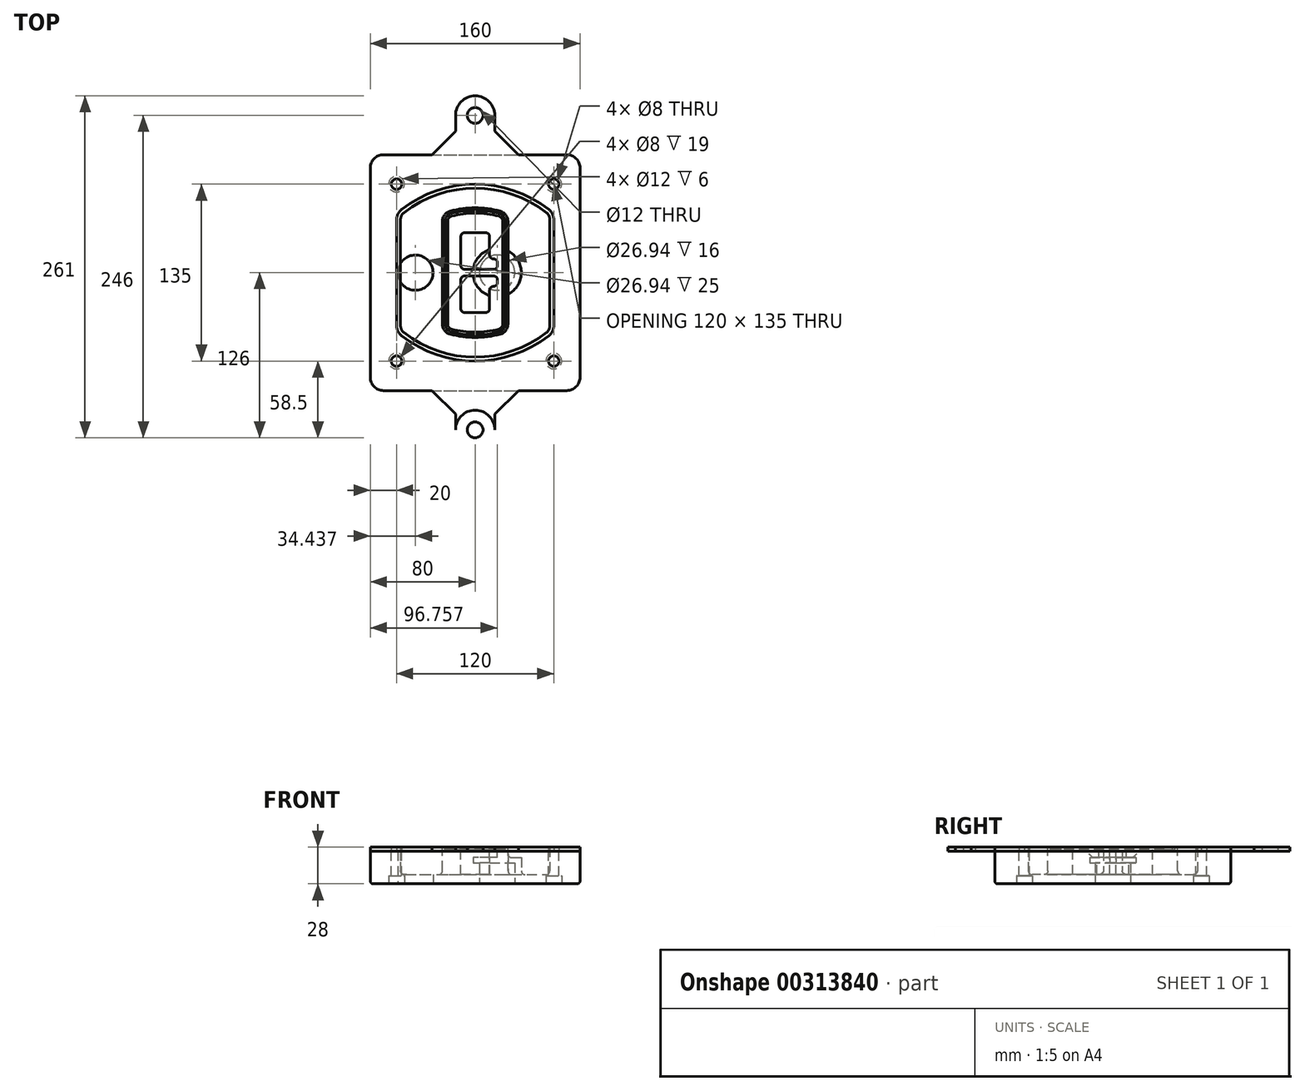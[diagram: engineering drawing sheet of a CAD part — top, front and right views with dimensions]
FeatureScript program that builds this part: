
annotation { "Feature Type Name" : "Feature", "Feature Type Description" : "" }
export const myFeature = defineFeature(function(context is Context, id is Id, definition is map)
    precondition{}
    {
        {
            var Q0;
            Q0=qCreatedBy(makeId("Top.planeOp"),FACE);
            var sketch = newSketch(context, id + "F0", { "sketchPlane" : qUnion([Q0])});
            skPoint(sketch, "E0.rect.middle", {"position": v(0, 0) * mm});
            skLineSegment(sketch, "E1.bottom", {"start": v(-70, -90) * mm, "end": v(70, -90) * mm});
            skLineSegment(sketch, "E1.top", {"start": v(-70, 90) * mm, "end": v(70, 90) * mm});
            skLineSegment(sketch, "E1.left", {"start": v(-80, -80) * mm, "end": v(-80, 80) * mm});
            skLineSegment(sketch, "E1.right", {"start": v(80, -80) * mm, "end": v(80, 80) * mm});
            skLineSegment(sketch, "E2", {"start": v(-80, 90) * mm, "end": v(80, -90) * mm, "construction": true});
            skLineSegment(sketch, "E3", {"start": v(80, 90) * mm, "end": v(-80, -90) * mm, "construction": true});
            skCircle(sketch, "E4", {"center": v(-60, 67.5) * mm, "radius": 4 * mm});
            skCircle(sketch, "E5", {"center": v(60, 67.5) * mm, "radius": 4 * mm});
            skCircle(sketch, "E6", {"center": v(60, -67.5) * mm, "radius": 4 * mm});
            skCircle(sketch, "E7", {"center": v(-60, -67.5) * mm, "radius": 4 * mm});
            skLineSegment(sketch, "E8", {"start": v(-60, 67.5) * mm, "end": v(60, 67.5) * mm, "construction": true});
            skLineSegment(sketch, "E9", {"start": v(60, 67.5) * mm, "end": v(60, -67.5) * mm, "construction": true});
            skLineSegment(sketch, "E10", {"start": v(60, -67.5) * mm, "end": v(-60, -67.5) * mm, "construction": true});
            skLineSegment(sketch, "E11", {"start": v(-60, -67.5) * mm, "end": v(-60, 67.5) * mm, "construction": true});
            skLineSegment(sketch, "E12", {"start": v(-60, 40.3) * mm, "end": v(-60, -40.3) * mm});
            skLineSegment(sketch, "E13", {"start": v(60, 40.3) * mm, "end": v(60, -40.3) * mm});
            skArc(sketch, "E14", {"start": v(56.15, 48.18) * mm, "mid": v(0, 67.5) * mm, "end": v(-56.15, 48.18) * mm});
            skArc(sketch, "E15", {"start": v(-56.15, -48.18) * mm, "mid": v(0, -67.5) * mm, "end": v(56.15, -48.18) * mm});
            skLineSegment(sketch, "E16", {"start": v(-60, 0) * mm, "end": v(60, 0) * mm, "construction": true});
            skPoint(sketch, "E17.visualSharp", {"position": v(-60, -45) * mm});
            skArc(sketch, "E17.filletArc", {"start": v(-60, -40.3) * mm, "mid": v(-58.99, -44.68) * mm, "end": v(-56.15, -48.18) * mm});
            skPoint(sketch, "E18.visualSharp", {"position": v(-60, 45) * mm});
            skArc(sketch, "E18.filletArc", {"start": v(-56.15, 48.18) * mm, "mid": v(-58.99, 44.68) * mm, "end": v(-60, 40.3) * mm});
            skPoint(sketch, "E19.visualSharp", {"position": v(60, 45) * mm});
            skArc(sketch, "E19.filletArc", {"start": v(60, 40.3) * mm, "mid": v(58.99, 44.68) * mm, "end": v(56.15, 48.18) * mm});
            skPoint(sketch, "E20.visualSharp", {"position": v(60, -45) * mm});
            skArc(sketch, "E20.filletArc", {"start": v(56.15, -48.18) * mm, "mid": v(58.99, -44.68) * mm, "end": v(60, -40.3) * mm});
            skPoint(sketch, "E21.visualSharp", {"position": v(-80, 90) * mm});
            skArc(sketch, "E21.filletArc", {"start": v(-70, 90) * mm, "mid": v(-77.07, 87.07) * mm, "end": v(-80, 80) * mm});
            skPoint(sketch, "E22.visualSharp", {"position": v(80, 90) * mm});
            skArc(sketch, "E22.filletArc", {"start": v(80, 80) * mm, "mid": v(77.07, 87.07) * mm, "end": v(70, 90) * mm});
            skPoint(sketch, "E23.visualSharp", {"position": v(80, -90) * mm});
            skArc(sketch, "E23.filletArc", {"start": v(70, -90) * mm, "mid": v(77.07, -87.07) * mm, "end": v(80, -80) * mm});
            skPoint(sketch, "E24.visualSharp", {"position": v(-80, -90) * mm});
            skArc(sketch, "E24.filletArc", {"start": v(-80, -80) * mm, "mid": v(-77.07, -87.07) * mm, "end": v(-70, -90) * mm});
            skArc(sketch, "E25.0", {"start": v(57, 40.3) * mm, "mid": v(56.3, 43.36) * mm, "end": v(54.3, 45.81) * mm});
            skLineSegment(sketch, "E25.1", {"start": v(57, 40.3) * mm, "end": v(57, -40.3) * mm});
            skArc(sketch, "E25.2", {"start": v(54.3, -45.81) * mm, "mid": v(56.3, -43.36) * mm, "end": v(57, -40.3) * mm});
            skArc(sketch, "E25.3", {"start": v(-54.3, -45.81) * mm, "mid": v(0, -64.5) * mm, "end": v(54.3, -45.81) * mm});
            skArc(sketch, "E25.4", {"start": v(-57, -40.3) * mm, "mid": v(-56.3, -43.36) * mm, "end": v(-54.3, -45.81) * mm});
            skArc(sketch, "E25.5", {"start": v(54.3, 45.81) * mm, "mid": v(0, 64.5) * mm, "end": v(-54.3, 45.81) * mm});
            skLineSegment(sketch, "E25.6", {"start": v(-57, 40.3) * mm, "end": v(-57, -40.3) * mm});
            skArc(sketch, "E25.7", {"start": v(-54.3, 45.81) * mm, "mid": v(-56.3, 43.36) * mm, "end": v(-57, 40.3) * mm});
            skArc(sketch, "E26.0", {"start": v(-58.62, 51.33) * mm, "mid": v(-62.58, 46.43) * mm, "end": v(-64, 40.3) * mm});
            skArc(sketch, "E26.1", {"start": v(58.62, 51.33) * mm, "mid": v(0, 71.5) * mm, "end": v(-58.62, 51.33) * mm});
            skArc(sketch, "E26.2", {"start": v(64, 40.3) * mm, "mid": v(62.58, 46.43) * mm, "end": v(58.62, 51.33) * mm});
            skLineSegment(sketch, "E26.3", {"start": v(64, 40.3) * mm, "end": v(64, -40.3) * mm});
            skArc(sketch, "E26.4", {"start": v(58.62, -51.33) * mm, "mid": v(62.58, -46.43) * mm, "end": v(64, -40.3) * mm});
            skLineSegment(sketch, "E26.5", {"start": v(-64, 40.3) * mm, "end": v(-64, -40.3) * mm});
            skArc(sketch, "E26.6", {"start": v(-58.62, -51.33) * mm, "mid": v(0, -71.5) * mm, "end": v(58.62, -51.33) * mm});
            skArc(sketch, "E26.7", {"start": v(-64, -40.3) * mm, "mid": v(-62.58, -46.43) * mm, "end": v(-58.62, -51.33) * mm});
            skSolve(sketch);
        }
        {
            var Q0;
            Q0=makeQuery(id+"F0.imprint","IMPRINT",FACE,{"disambiguationData":[TD([[makeQuery(id+"F0.imprint","IMPRINT",EDGE,{"derivedFrom":sQuery(id+"F0.wireOp",EDGE,"E1.bottom")}),1.0]])]});
            var Q1;
            Q1=makeQuery(id+"F0.imprint","IMPRINT",FACE,{"disambiguationData":[TD([[makeQuery(id+"F0.imprint","IMPRINT",EDGE,{"derivedFrom":sQuery(id+"F0.wireOp",EDGE,"E12")}),1.0]])]});
            var Q2;
            Q2=makeQuery(id+"F0.imprint","IMPRINT",FACE,{"disambiguationData":[TD([[makeQuery(id+"F0.imprint","IMPRINT",EDGE,{"derivedFrom":sQuery(id+"F0.wireOp",EDGE,"E25.0")}),1.0]])]});
            var Q3;
            Q3=makeQuery(id+"F0.imprint","IMPRINT",FACE,{"disambiguationData":[TD([[makeQuery(id+"F0.imprint","IMPRINT",EDGE,{"derivedFrom":sQuery(id+"F0.wireOp",EDGE,"E12")}),-1.0]])]});
            extrude(context, id + "F1", {"entities" : qUnion([Q0, Q1, Q2, Q3]), "oppositeDirection" : true, "depth" : 25 * mm});
        }
        {
            var Q0;
            Q0=makeQuery(id+"F0.imprint","IMPRINT",FACE,{"disambiguationData":[TD([[makeQuery(id+"F0.imprint","IMPRINT",EDGE,{"derivedFrom":sQuery(id+"F0.wireOp",EDGE,"E12")}),1.0]])]});
            extrude(context, id + "F2", {"entities" : qUnion([Q0]), "operationType" : NewBodyOperationType.ADD, "depth" : 3 * mm});
        }
        {
            var Q0;
            Q0=makeQuery(id+"F0.imprint","IMPRINT",FACE,{"disambiguationData":[TD([[makeQuery(id+"F0.imprint","IMPRINT",EDGE,{"derivedFrom":sQuery(id+"F0.wireOp",EDGE,"E25.0")}),1.0]])]});
            extrude(context, id + "F3", {"entities" : qUnion([Q0]), "operationType" : NewBodyOperationType.REMOVE, "oppositeDirection" : true, "depth" : 18 * mm});
        }
        {
            var Q0;
            Q0=makeQuery(id+"F2.opExtrude","CAP_FACE",FACE,{"disambiguationData":[OSD([sQuery(id+"F0.wireOp",EDGE,"E12"),sQuery(id+"F0.wireOp",EDGE,"E13"),sQuery(id+"F0.wireOp",EDGE,"E14"),sQuery(id+"F0.wireOp",EDGE,"E15"),sQuery(id+"F0.wireOp",EDGE,"E17.filletArc"),sQuery(id+"F0.wireOp",EDGE,"E18.filletArc"),sQuery(id+"F0.wireOp",EDGE,"E19.filletArc"),sQuery(id+"F0.wireOp",EDGE,"E20.filletArc"),sQuery(id+"F0.wireOp",EDGE,"E25.0"),sQuery(id+"F0.wireOp",EDGE,"E25.1"),sQuery(id+"F0.wireOp",EDGE,"E25.2"),sQuery(id+"F0.wireOp",EDGE,"E25.3"),sQuery(id+"F0.wireOp",EDGE,"E25.4"),sQuery(id+"F0.wireOp",EDGE,"E25.5"),sQuery(id+"F0.wireOp",EDGE,"E25.6"),sQuery(id+"F0.wireOp",EDGE,"E25.7")])],"isStart":false});
            var sketch = newSketch(context, id + "F4", { "sketchPlane" : qUnion([Q0])});
            skArc(sketch, "E27.0", {"start": v(-19.08, -46.97) * mm, "mid": v(0, -49.5) * mm, "end": v(19.08, -46.97) * mm});
            skArc(sketch, "E28.0", {"start": v(19.08, 46.97) * mm, "mid": v(0, 49.5) * mm, "end": v(-19.08, 46.97) * mm});
            skLineSegment(sketch, "E29", {"start": v(-25, 39.25) * mm, "end": v(-25, -39.25) * mm});
            skLineSegment(sketch, "E30", {"start": v(25, 39.25) * mm, "end": v(25, -39.25) * mm});
            skLineSegment(sketch, "E31", {"start": v(-25, 45.1) * mm, "end": v(25, 45.1) * mm, "construction": true});
            skLineSegment(sketch, "E32", {"start": v(-25, -45.1) * mm, "end": v(25, -45.1) * mm, "construction": true});
            skPoint(sketch, "E33.visualSharp", {"position": v(-25, 45.1) * mm});
            skArc(sketch, "E33.filletArc", {"start": v(-19.08, 46.97) * mm, "mid": v(-23.35, 44.11) * mm, "end": v(-25, 39.25) * mm});
            skPoint(sketch, "E34.visualSharp", {"position": v(25, 45.1) * mm});
            skArc(sketch, "E34.filletArc", {"start": v(25, 39.25) * mm, "mid": v(23.35, 44.11) * mm, "end": v(19.08, 46.97) * mm});
            skPoint(sketch, "E35.visualSharp", {"position": v(25, -45.1) * mm});
            skArc(sketch, "E35.filletArc", {"start": v(19.08, -46.97) * mm, "mid": v(23.35, -44.11) * mm, "end": v(25, -39.25) * mm});
            skPoint(sketch, "E36.visualSharp", {"position": v(-25, -45.1) * mm});
            skArc(sketch, "E36.filletArc", {"start": v(-25, -39.25) * mm, "mid": v(-23.35, -44.11) * mm, "end": v(-19.08, -46.97) * mm});
            skArc(sketch, "E37.0", {"start": v(54.3, 45.81) * mm, "mid": v(0, 64.5) * mm, "end": v(-54.3, 45.81) * mm});
            skArc(sketch, "E37.1", {"start": v(-54.3, 45.81) * mm, "mid": v(-56.3, 43.36) * mm, "end": v(-57, 40.3) * mm});
            skLineSegment(sketch, "E37.2", {"start": v(-57, 40.3) * mm, "end": v(-57, -40.3) * mm});
            skArc(sketch, "E37.3", {"start": v(-57, -40.3) * mm, "mid": v(-56.3, -43.36) * mm, "end": v(-54.3, -45.81) * mm});
            skArc(sketch, "E37.4", {"start": v(-54.3, -45.81) * mm, "mid": v(0, -64.5) * mm, "end": v(54.3, -45.81) * mm});
            skArc(sketch, "E37.5", {"start": v(54.3, -45.81) * mm, "mid": v(56.3, -43.36) * mm, "end": v(57, -40.3) * mm});
            skLineSegment(sketch, "E37.6", {"start": v(57, 40.3) * mm, "end": v(57, -40.3) * mm});
            skArc(sketch, "E37.7", {"start": v(57, 40.3) * mm, "mid": v(56.3, 43.36) * mm, "end": v(54.3, 45.81) * mm});
            skLineSegment(sketch, "E38.0", {"start": v(23, 39.25) * mm, "end": v(23, -39.25) * mm});
            skArc(sketch, "E38.1", {"start": v(18.56, -45.04) * mm, "mid": v(21.76, -42.9) * mm, "end": v(23, -39.25) * mm});
            skArc(sketch, "E38.2", {"start": v(-18.56, -45.04) * mm, "mid": v(0, -47.5) * mm, "end": v(18.56, -45.04) * mm});
            skArc(sketch, "E38.3", {"start": v(-23, -39.25) * mm, "mid": v(-21.76, -42.9) * mm, "end": v(-18.56, -45.04) * mm});
            skLineSegment(sketch, "E38.4", {"start": v(-23, 39.25) * mm, "end": v(-23, -39.25) * mm});
            skArc(sketch, "E38.5", {"start": v(23, 39.25) * mm, "mid": v(21.76, 42.9) * mm, "end": v(18.56, 45.04) * mm});
            skArc(sketch, "E38.6", {"start": v(-18.56, 45.04) * mm, "mid": v(-21.76, 42.9) * mm, "end": v(-23, 39.25) * mm});
            skArc(sketch, "E38.7", {"start": v(18.56, 45.04) * mm, "mid": v(0, 47.5) * mm, "end": v(-18.56, 45.04) * mm});
            skArc(sketch, "E39.0", {"start": v(21, 39.25) * mm, "mid": v(20.18, 41.68) * mm, "end": v(18.04, 43.1) * mm});
            skLineSegment(sketch, "E39.1", {"start": v(21, 39.25) * mm, "end": v(21, -39.25) * mm});
            skArc(sketch, "E39.2", {"start": v(18.04, -43.1) * mm, "mid": v(20.18, -41.68) * mm, "end": v(21, -39.25) * mm});
            skArc(sketch, "E39.3", {"start": v(-18.04, -43.1) * mm, "mid": v(0, -45.5) * mm, "end": v(18.04, -43.1) * mm});
            skArc(sketch, "E39.4", {"start": v(-21, -39.25) * mm, "mid": v(-20.18, -41.68) * mm, "end": v(-18.04, -43.1) * mm});
            skArc(sketch, "E39.5", {"start": v(18.04, 43.1) * mm, "mid": v(0, 45.5) * mm, "end": v(-18.04, 43.1) * mm});
            skLineSegment(sketch, "E39.6", {"start": v(-21, 39.25) * mm, "end": v(-21, -39.25) * mm});
            skArc(sketch, "E39.7", {"start": v(-18.04, 43.1) * mm, "mid": v(-20.18, 41.68) * mm, "end": v(-21, 39.25) * mm});
            skLineSegment(sketch, "E40", {"start": v(-25, 0) * mm, "end": v(25, 0) * mm, "construction": true});
            skLineSegment(sketch, "E41", {"start": v(-11, 5.5) * mm, "end": v(-11, 27.5) * mm});
            skLineSegment(sketch, "E42", {"start": v(-8, 30.5) * mm, "end": v(8, 30.5) * mm});
            skLineSegment(sketch, "E43", {"start": v(11, 27.5) * mm, "end": v(11, 13.5) * mm});
            skLineSegment(sketch, "E44", {"start": v(14, 10.5) * mm, "end": v(14, 10.5) * mm});
            skLineSegment(sketch, "E45", {"start": v(17, 7.5) * mm, "end": v(17, 5.5) * mm});
            skLineSegment(sketch, "E46", {"start": v(14, 2.5) * mm, "end": v(-8, 2.5) * mm});
            skPoint(sketch, "E47.visualSharp", {"position": v(-11, 30.5) * mm});
            skArc(sketch, "E47.filletArc", {"start": v(-8, 30.5) * mm, "mid": v(-10.12, 29.62) * mm, "end": v(-11, 27.5) * mm});
            skPoint(sketch, "E48.visualSharp", {"position": v(11, 30.5) * mm});
            skArc(sketch, "E48.filletArc", {"start": v(11, 27.5) * mm, "mid": v(10.12, 29.62) * mm, "end": v(8, 30.5) * mm});
            skPoint(sketch, "E49.visualSharp", {"position": v(11, 10.5) * mm});
            skArc(sketch, "E49.filletArc", {"start": v(11, 13.5) * mm, "mid": v(11.88, 11.38) * mm, "end": v(14, 10.5) * mm});
            skPoint(sketch, "E50.visualSharp", {"position": v(17, 10.5) * mm});
            skArc(sketch, "E50.filletArc", {"start": v(17, 7.5) * mm, "mid": v(16.12, 9.62) * mm, "end": v(14, 10.5) * mm});
            skPoint(sketch, "E51.visualSharp", {"position": v(17, 2.5) * mm});
            skArc(sketch, "E51.filletArc", {"start": v(14, 2.5) * mm, "mid": v(16.12, 3.38) * mm, "end": v(17, 5.5) * mm});
            skPoint(sketch, "E52.visualSharp", {"position": v(-11, 2.5) * mm});
            skArc(sketch, "E52.filletArc", {"start": v(-11, 5.5) * mm, "mid": v(-10.12, 3.38) * mm, "end": v(-8, 2.5) * mm});
            skLineSegment(sketch, "E53.0.MirrorCS", {"start": v(14, -2.5) * mm, "end": v(-8, -2.5) * mm});
            skArc(sketch, "E54.0.MirrorCS", {"start": v(-11, -5.5) * mm, "mid": v(-10.12, -3.38) * mm, "end": v(-8, -2.5) * mm});
            skLineSegment(sketch, "E55.0.MirrorCS", {"start": v(-11, -5.5) * mm, "end": v(-11, -27.5) * mm});
            skArc(sketch, "E56.0.MirrorCS", {"start": v(-8, -30.5) * mm, "mid": v(-10.12, -29.62) * mm, "end": v(-11, -27.5) * mm});
            skLineSegment(sketch, "E57.0.MirrorCS", {"start": v(-8, -30.5) * mm, "end": v(8, -30.5) * mm});
            skArc(sketch, "E58.0.MirrorCS", {"start": v(11, -27.5) * mm, "mid": v(10.12, -29.62) * mm, "end": v(8, -30.5) * mm});
            skLineSegment(sketch, "E59.0.MirrorCS", {"start": v(11, -27.5) * mm, "end": v(11, -13.5) * mm});
            skArc(sketch, "E60.0.MirrorCS", {"start": v(11, -13.5) * mm, "mid": v(11.88, -11.38) * mm, "end": v(14, -10.5) * mm});
            skArc(sketch, "E61.0.MirrorCS", {"start": v(17, -7.5) * mm, "mid": v(16.12, -9.62) * mm, "end": v(14, -10.5) * mm});
            skLineSegment(sketch, "E62.0.MirrorCS", {"start": v(17, -7.5) * mm, "end": v(17, -5.5) * mm});
            skArc(sketch, "E63.0.MirrorCS", {"start": v(14, -2.5) * mm, "mid": v(16.12, -3.38) * mm, "end": v(17, -5.5) * mm});
            skSolve(sketch);
        }
        {
            var Q0;
            Q0=makeQuery(id+"F4.imprint","IMPRINT",FACE,{"disambiguationData":[TD([[makeQuery(id+"F4.imprint","IMPRINT",EDGE,{"derivedFrom":sQuery(id+"F4.wireOp",EDGE,"E27.0")}),1.0]])]});
            var Q1;
            Q1=makeQuery(id+"F4.imprint","IMPRINT",FACE,{"disambiguationData":[TD([[makeQuery(id+"F4.imprint","IMPRINT",EDGE,{"derivedFrom":sQuery(id+"F4.wireOp",EDGE,"E38.0")}),-1.0]])]});
            var Q2;
            Q2=makeQuery(id+"F4.imprint","IMPRINT",FACE,{"disambiguationData":[TD([[makeQuery(id+"F4.imprint","IMPRINT",EDGE,{"derivedFrom":sQuery(id+"F4.wireOp",EDGE,"E39.0")}),1.0]])]});
            extrude(context, id + "F5", {"entities" : qUnion([Q0, Q1, Q2]), "operationType" : NewBodyOperationType.ADD, "endBound" : BoundingType.UP_TO_NEXT, "oppositeDirection" : true, "depth" : 25 * mm});
        }
        {
            var Q0;
            Q0=makeQuery(id+"F4.imprint","IMPRINT",FACE,{"disambiguationData":[TD([[makeQuery(id+"F4.imprint","IMPRINT",EDGE,{"derivedFrom":sQuery(id+"F4.wireOp",EDGE,"E38.0")}),-1.0]])]});
            extrude(context, id + "F6", {"entities" : qUnion([Q0]), "operationType" : NewBodyOperationType.REMOVE, "oppositeDirection" : true, "depth" : 2 * mm});
        }
        {
            var Q0;
            Q0=makeQuery(id+"F1.opExtrude","CAP_FACE",FACE,{"disambiguationData":[OSD([sQuery(id+"F0.wireOp",EDGE,"E1.bottom"),sQuery(id+"F0.wireOp",EDGE,"E1.top"),sQuery(id+"F0.wireOp",EDGE,"E1.left"),sQuery(id+"F0.wireOp",EDGE,"E1.right"),sQuery(id+"F0.wireOp",EDGE,"E4"),sQuery(id+"F0.wireOp",EDGE,"E5"),sQuery(id+"F0.wireOp",EDGE,"E6"),sQuery(id+"F0.wireOp",EDGE,"E7"),sQuery(id+"F0.wireOp",EDGE,"E21.filletArc"),sQuery(id+"F0.wireOp",EDGE,"E22.filletArc"),sQuery(id+"F0.wireOp",EDGE,"E23.filletArc"),sQuery(id+"F0.wireOp",EDGE,"E24.filletArc")])],"isStart":false});
            var sketch = newSketch(context, id + "F7", { "sketchPlane" : qUnion([Q0])});
            skCircle(sketch, "E64", {"center": v(16.76, 0) * mm, "radius": 13.47 * mm});
            skCircle(sketch, "E65", {"center": v(-45.56, 0) * mm, "radius": 13.47 * mm});
            skLineSegment(sketch, "E66", {"start": v(80, 0) * mm, "end": v(-80, 0) * mm});
            skCircle(sketch, "E67", {"center": v(16.76, 0) * mm, "radius": 18.47 * mm});
            skCircle(sketch, "E68", {"center": v(60, -67.5) * mm, "radius": 6 * mm});
            skCircle(sketch, "E69", {"center": v(-60, -67.5) * mm, "radius": 6 * mm});
            skCircle(sketch, "E70", {"center": v(-60, 67.5) * mm, "radius": 6 * mm});
            skCircle(sketch, "E71", {"center": v(60, 67.5) * mm, "radius": 6 * mm});
            skSolve(sketch);
        }
        {
            var Q0;
            {var subQ1=sQuery(id+"F7.wireOp",EDGE,"E66");var subQ4=sQuery(id+"F7.wireOp",EDGE,"E64");var subQ6=makeQuery(id+"F7.imprint","INTERSECT",VERTEX,{"disambiguationData":[OD(0.0)],"derivedFrom":[subQ4,subQ1]});Q0=makeQuery(id+"F7.imprint","IMPRINT",FACE,{"disambiguationData":[TD([[makeQuery(id+"F7.imprint","IMPRINT",EDGE,{"disambiguationData":[TD([[subQ6,-1.0]])],"derivedFrom":subQ4}),-1.0]])]});}
            var Q1;
            {var subQ0=sQuery(id+"F7.wireOp",EDGE,"E66");var subQ1=sQuery(id+"F7.wireOp",EDGE,"E64");var subQ3=makeQuery(id+"F7.imprint","INTERSECT",VERTEX,{"disambiguationData":[OD(0.0)],"derivedFrom":[subQ1,subQ0]});Q1=makeQuery(id+"F7.imprint","IMPRINT",FACE,{"disambiguationData":[TD([[makeQuery(id+"F7.imprint","IMPRINT",EDGE,{"disambiguationData":[TD([[subQ3,-1.0]])],"derivedFrom":subQ1}),1.0]])]});}
            var Q2;
            {var subQ0=sQuery(id+"F7.wireOp",EDGE,"E66");var subQ1=sQuery(id+"F7.wireOp",EDGE,"E64");var subQ3=makeQuery(id+"F7.imprint","INTERSECT",VERTEX,{"disambiguationData":[OD(0.0)],"derivedFrom":[subQ1,subQ0]});Q2=makeQuery(id+"F7.imprint","IMPRINT",FACE,{"disambiguationData":[TD([[makeQuery(id+"F7.imprint","IMPRINT",EDGE,{"disambiguationData":[TD([[subQ3,1.0]])],"derivedFrom":subQ1}),1.0]])]});}
            var Q3;
            {var subQ1=sQuery(id+"F7.wireOp",EDGE,"E66");var subQ4=sQuery(id+"F7.wireOp",EDGE,"E64");var subQ6=makeQuery(id+"F7.imprint","INTERSECT",VERTEX,{"disambiguationData":[OD(0.0)],"derivedFrom":[subQ4,subQ1]});Q3=makeQuery(id+"F7.imprint","IMPRINT",FACE,{"disambiguationData":[TD([[makeQuery(id+"F7.imprint","IMPRINT",EDGE,{"disambiguationData":[TD([[subQ6,1.0]])],"derivedFrom":subQ4}),-1.0]])]});}
            extrude(context, id + "F8", {"entities" : qUnion([Q0, Q1, Q2, Q3]), "operationType" : NewBodyOperationType.ADD, "oppositeDirection" : true, "depth" : 20 * mm});
        }
        {
            var Q0;
            {var subQ0=sQuery(id+"F7.wireOp",EDGE,"E66");var subQ1=sQuery(id+"F7.wireOp",EDGE,"E64");var subQ3=makeQuery(id+"F7.imprint","INTERSECT",VERTEX,{"disambiguationData":[OD(0.0)],"derivedFrom":[subQ1,subQ0]});Q0=makeQuery(id+"F7.imprint","IMPRINT",FACE,{"disambiguationData":[TD([[makeQuery(id+"F7.imprint","IMPRINT",EDGE,{"disambiguationData":[TD([[subQ3,-1.0]])],"derivedFrom":subQ1}),1.0]])]});}
            var Q1;
            {var subQ0=sQuery(id+"F7.wireOp",EDGE,"E66");var subQ1=sQuery(id+"F7.wireOp",EDGE,"E64");var subQ3=makeQuery(id+"F7.imprint","INTERSECT",VERTEX,{"disambiguationData":[OD(0.0)],"derivedFrom":[subQ1,subQ0]});Q1=makeQuery(id+"F7.imprint","IMPRINT",FACE,{"disambiguationData":[TD([[makeQuery(id+"F7.imprint","IMPRINT",EDGE,{"disambiguationData":[TD([[subQ3,1.0]])],"derivedFrom":subQ1}),1.0]])]});}
            extrude(context, id + "F9", {"entities" : qUnion([Q0, Q1]), "operationType" : NewBodyOperationType.REMOVE, "oppositeDirection" : true, "depth" : 16 * mm});
        }
        {
            var Q0;
            {var subQ0=sQuery(id+"F7.wireOp",EDGE,"E66");var subQ1=sQuery(id+"F7.wireOp",EDGE,"E65");var subQ3=makeQuery(id+"F7.imprint","INTERSECT",VERTEX,{"disambiguationData":[OD(0.0)],"derivedFrom":[subQ1,subQ0]});Q0=makeQuery(id+"F7.imprint","IMPRINT",FACE,{"disambiguationData":[TD([[makeQuery(id+"F7.imprint","IMPRINT",EDGE,{"disambiguationData":[TD([[subQ3,-1.0]])],"derivedFrom":subQ1}),1.0]])]});}
            var Q1;
            {var subQ0=sQuery(id+"F7.wireOp",EDGE,"E66");var subQ1=sQuery(id+"F7.wireOp",EDGE,"E65");var subQ3=makeQuery(id+"F7.imprint","INTERSECT",VERTEX,{"disambiguationData":[OD(0.0)],"derivedFrom":[subQ1,subQ0]});Q1=makeQuery(id+"F7.imprint","IMPRINT",FACE,{"disambiguationData":[TD([[makeQuery(id+"F7.imprint","IMPRINT",EDGE,{"disambiguationData":[TD([[subQ3,1.0]])],"derivedFrom":subQ1}),1.0]])]});}
            extrude(context, id + "F10", {"entities" : qUnion([Q0, Q1]), "operationType" : NewBodyOperationType.REMOVE, "oppositeDirection" : true, "depth" : 25 * mm});
        }
        {
            var Q0;
            Q0=makeQuery(id+"F7.imprint","IMPRINT",FACE,{"disambiguationData":[TD([[makeQuery(id+"F7.imprint","IMPRINT",EDGE,{"derivedFrom":sQuery(id+"F7.wireOp",EDGE,"E68")}),1.0]])]});
            var Q1;
            Q1=makeQuery(id+"F7.imprint","IMPRINT",FACE,{"disambiguationData":[TD([[makeQuery(id+"F7.imprint","IMPRINT",EDGE,{"derivedFrom":makeQuery(id+"F1.opExtrude","CAP_EDGE",EDGE,{"disambiguationData":[OSD([sQuery(id+"F0.wireOp",EDGE,"E5")])],"isStart":false})}),-1.0]])]});
            var Q2;
            Q2=makeQuery(id+"F7.imprint","IMPRINT",FACE,{"disambiguationData":[TD([[makeQuery(id+"F7.imprint","IMPRINT",EDGE,{"derivedFrom":sQuery(id+"F7.wireOp",EDGE,"E69")}),1.0]])]});
            var Q3;
            Q3=makeQuery(id+"F7.imprint","IMPRINT",FACE,{"disambiguationData":[TD([[makeQuery(id+"F7.imprint","IMPRINT",EDGE,{"derivedFrom":makeQuery(id+"F1.opExtrude","CAP_EDGE",EDGE,{"disambiguationData":[OSD([sQuery(id+"F0.wireOp",EDGE,"E4")])],"isStart":false})}),-1.0]])]});
            var Q4;
            Q4=makeQuery(id+"F7.imprint","IMPRINT",FACE,{"disambiguationData":[TD([[makeQuery(id+"F7.imprint","IMPRINT",EDGE,{"derivedFrom":sQuery(id+"F7.wireOp",EDGE,"E70")}),1.0]])]});
            var Q5;
            Q5=makeQuery(id+"F7.imprint","IMPRINT",FACE,{"disambiguationData":[TD([[makeQuery(id+"F7.imprint","IMPRINT",EDGE,{"derivedFrom":makeQuery(id+"F1.opExtrude","CAP_EDGE",EDGE,{"disambiguationData":[OSD([sQuery(id+"F0.wireOp",EDGE,"E7")])],"isStart":false})}),-1.0]])]});
            var Q6;
            Q6=makeQuery(id+"F7.imprint","IMPRINT",FACE,{"disambiguationData":[TD([[makeQuery(id+"F7.imprint","IMPRINT",EDGE,{"derivedFrom":sQuery(id+"F7.wireOp",EDGE,"E71")}),1.0]])]});
            var Q7;
            Q7=makeQuery(id+"F7.imprint","IMPRINT",FACE,{"disambiguationData":[TD([[makeQuery(id+"F7.imprint","IMPRINT",EDGE,{"derivedFrom":makeQuery(id+"F1.opExtrude","CAP_EDGE",EDGE,{"disambiguationData":[OSD([sQuery(id+"F0.wireOp",EDGE,"E6")])],"isStart":false})}),-1.0]])]});
            extrude(context, id + "F11", {"entities" : qUnion([Q0, Q1, Q2, Q3, Q4, Q5, Q6, Q7]), "operationType" : NewBodyOperationType.REMOVE, "oppositeDirection" : true, "depth" : 6 * mm});
        }
        {
            var Q0;
            Q0=makeQuery(id+"F9.boolean.opBoolean","COPY",FACE,{"derivedFrom":makeQuery(id+"F9.opExtrude","CAP_FACE",FACE,{"disambiguationData":[OSD([sQuery(id+"F7.wireOp",EDGE,"E64")])],"isStart":false})});
            var sketch = newSketch(context, id + "F12", { "sketchPlane" : qUnion([Q0])});
            skArc(sketch, "E72.0", {"start": v(11, 17.55) * mm, "mid": v(2.57, 11.82) * mm, "end": v(-1.54, 2.5) * mm});
            skArc(sketch, "E72.1", {"start": v(-1.54, -2.5) * mm, "mid": v(2.57, -11.82) * mm, "end": v(11, -17.55) * mm});
            skLineSegment(sketch, "E73", {"start": v(-1.54, -2.5) * mm, "end": v(14, -2.5) * mm});
            skLineSegment(sketch, "E74.0", {"start": v(14, 2.5) * mm, "end": v(-1.54, 2.5) * mm});
            skArc(sketch, "E74.1", {"start": v(14, 2.5) * mm, "mid": v(16.12, 3.38) * mm, "end": v(17, 5.5) * mm});
            skLineSegment(sketch, "E74.2", {"start": v(17, 7.5) * mm, "end": v(17, 5.5) * mm});
            skArc(sketch, "E74.3", {"start": v(17, 7.5) * mm, "mid": v(16.12, 9.62) * mm, "end": v(14, 10.5) * mm});
            skArc(sketch, "E74.4", {"start": v(11, 13.5) * mm, "mid": v(11.88, 11.38) * mm, "end": v(14, 10.5) * mm});
            skLineSegment(sketch, "E74.5", {"start": v(11, 17.55) * mm, "end": v(11, 13.5) * mm});
            skLineSegment(sketch, "E74.7", {"start": v(14, -2.5) * mm, "end": v(-1.54, -2.5) * mm});
            skArc(sketch, "E74.8", {"start": v(14, -2.5) * mm, "mid": v(16.12, -3.38) * mm, "end": v(17, -5.5) * mm});
            skLineSegment(sketch, "E74.9", {"start": v(17, -7.5) * mm, "end": v(17, -5.5) * mm});
            skArc(sketch, "E74.10", {"start": v(17, -7.5) * mm, "mid": v(16.12, -9.62) * mm, "end": v(14, -10.5) * mm});
            skArc(sketch, "E74.11", {"start": v(11, -13.5) * mm, "mid": v(11.88, -11.38) * mm, "end": v(14, -10.5) * mm});
            skLineSegment(sketch, "E74.12", {"start": v(11, -17.55) * mm, "end": v(11, -13.5) * mm});
            skPoint(sketch, "E75.orphan", {"position": v(11, -27.5) * mm});
            skPoint(sketch, "E76.orphan", {"position": v(-8, -2.5) * mm});
            skPoint(sketch, "E77.orphan", {"position": v(-8, 2.5) * mm});
            skPoint(sketch, "E78.orphan", {"position": v(11, 27.5) * mm});
            skSolve(sketch);
        }
        {
            var Q0;
            {var subQ7=sQuery(id+"F12.wireOp",EDGE,"E72.0");var subQ14=sQuery(id+"F12.wireOp",EDGE,"E72.1");var subQ16=sQuery(id+"F12.wireOp",EDGE,"E74.1");var subQ18=sQuery(id+"F12.wireOp",EDGE,"E74.8");Q0=qUnion([makeQuery(id+"F12.imprint","IMPRINT",FACE,{"disambiguationData":[TD([[makeQuery(id+"F12.imprint","IMPRINT",EDGE,{"derivedFrom":subQ7}),1.0]])]}),makeQuery(id+"F12.imprint","IMPRINT",FACE,{"disambiguationData":[TD([[makeQuery(id+"F12.imprint","IMPRINT",EDGE,{"derivedFrom":subQ14}),1.0]])]}),makeQuery(id+"F12.imprint","IMPRINT",FACE,{"disambiguationData":[TD([[makeQuery(id+"F12.imprint","IMPRINT",EDGE,{"derivedFrom":subQ16}),1.0]])]}),makeQuery(id+"F12.imprint","IMPRINT",FACE,{"disambiguationData":[TD([[makeQuery(id+"F12.imprint","IMPRINT",EDGE,{"derivedFrom":subQ18}),-1.0]])]})]);}
            var Q1;
            Q1=makeQuery(id+"F5.boolean.opBoolean","SPLIT",FACE,{"disambiguationData":[TD([makeQuery(id+"F5.opExtrude","SWEPT_FACE",FACE,{"disambiguationData":[OSD([sQuery(id+"F4.wireOp",EDGE,"E41")])]})])],"derivedFrom":makeQuery(id+"F3.boolean.opBoolean","COPY",FACE,{"derivedFrom":makeQuery(id+"F3.opExtrude","CAP_FACE",FACE,{"disambiguationData":[OSD([sQuery(id+"F0.wireOp",EDGE,"E25.0"),sQuery(id+"F0.wireOp",EDGE,"E25.1"),sQuery(id+"F0.wireOp",EDGE,"E25.2"),sQuery(id+"F0.wireOp",EDGE,"E25.3"),sQuery(id+"F0.wireOp",EDGE,"E25.4"),sQuery(id+"F0.wireOp",EDGE,"E25.5"),sQuery(id+"F0.wireOp",EDGE,"E25.6"),sQuery(id+"F0.wireOp",EDGE,"E25.7")])],"isStart":false})})});
            extrude(context, id + "F13", {"entities" : qUnion([Q0]), "operationType" : NewBodyOperationType.REMOVE, "endBound" : BoundingType.UP_TO_SURFACE, "endBoundEntityFace" : qUnion([Q1]), "depth" : 25 * mm});
        }
        {
            var Q0;
            Q0=makeQuery(id+"F3.boolean.opBoolean","COPY",EDGE,{"derivedFrom":makeQuery(id+"F3.opExtrude","CAP_EDGE",EDGE,{"disambiguationData":[OSD([sQuery(id+"F0.wireOp",EDGE,"E25.6")])],"isStart":false})});
            var Q1;
            Q1=makeQuery(id+"F8.boolean.opBoolean","INTERSECT",EDGE,{"derivedFrom":[makeQuery(id+"F5.opExtrude","SWEPT_FACE",FACE,{"disambiguationData":[OSD([sQuery(id+"F4.wireOp",EDGE,"E30")])]}),makeQuery(id+"F8.opExtrude","CAP_FACE",FACE,{"disambiguationData":[OSD([sQuery(id+"F7.wireOp",EDGE,"E67")])],"isStart":false})]});
            var Q2;
            Q2=makeQuery(id+"F8.boolean.opBoolean","INTERSECT",EDGE,{"disambiguationData":[OD(1.0)],"derivedFrom":[makeQuery(id+"F5.opExtrude","SWEPT_FACE",FACE,{"disambiguationData":[OSD([sQuery(id+"F4.wireOp",EDGE,"E30")])]}),makeQuery(id+"F8.opExtrude","SWEPT_FACE",FACE,{"disambiguationData":[OSD([sQuery(id+"F7.wireOp",EDGE,"E67")])]})]});
            var Q3;
            {var subQ0=sQuery(id+"F4.wireOp",EDGE,"E30");Q3=makeQuery(id+"F8.boolean.opBoolean","SPLIT",EDGE,{"disambiguationData":[TD([makeQuery(id+"F5.opExtrude","SWEPT_FACE",FACE,{"disambiguationData":[OSD([sQuery(id+"F4.wireOp",EDGE,"E35.filletArc")])]})])],"derivedFrom":makeQuery(id+"F5.opExtrude","CAP_EDGE",EDGE,{"disambiguationData":[OSD([subQ0])],"isStart":false})});}
            var Q4;
            {var subQ0=sQuery(id+"F0.wireOp",EDGE,"E25.7");var subQ1=sQuery(id+"F0.wireOp",EDGE,"E25.1");var subQ2=sQuery(id+"F0.wireOp",EDGE,"E25.6");var subQ3=sQuery(id+"F0.wireOp",EDGE,"E25.5");var subQ4=sQuery(id+"F0.wireOp",EDGE,"E25.4");var subQ5=sQuery(id+"F0.wireOp",EDGE,"E25.0");var subQ6=sQuery(id+"F0.wireOp",EDGE,"E25.2");var subQ7=sQuery(id+"F0.wireOp",EDGE,"E25.3");Q4=makeQuery(id+"F8.boolean.opBoolean","INTERSECT",EDGE,{"derivedFrom":[makeQuery(id+"F5.boolean.opBoolean","SPLIT",FACE,{"disambiguationData":[TD([makeQuery(id+"F2.opExtrude","SWEPT_FACE",FACE,{"disambiguationData":[OSD([subQ5])]})])],"derivedFrom":makeQuery(id+"F3.boolean.opBoolean","COPY",FACE,{"derivedFrom":makeQuery(id+"F3.opExtrude","CAP_FACE",FACE,{"disambiguationData":[OSD([subQ5,subQ1,subQ6,subQ7,subQ4,subQ3,subQ2,subQ0])],"isStart":false})})}),makeQuery(id+"F8.opExtrude","SWEPT_FACE",FACE,{"disambiguationData":[OSD([sQuery(id+"F7.wireOp",EDGE,"E67")])]})]});}
            var Q5;
            Q5=makeQuery(id+"F8.boolean.opBoolean","INTERSECT",EDGE,{"disambiguationData":[OD(0.0)],"derivedFrom":[makeQuery(id+"F5.opExtrude","SWEPT_FACE",FACE,{"disambiguationData":[OSD([sQuery(id+"F4.wireOp",EDGE,"E30")])]}),makeQuery(id+"F8.opExtrude","SWEPT_FACE",FACE,{"disambiguationData":[OSD([sQuery(id+"F7.wireOp",EDGE,"E67")])]})]});
            fillet(context, id + "F14", {"entities" : qUnion([Q0, Q1, Q2, Q3, Q4, Q5]), "radius" : 3 * mm, "tangentPropagation" : true, "allowEdgeOverflow" : false});
        }
        {
            var Q0;
            Q0=makeQuery(id+"F1.opExtrude","CAP_EDGE",EDGE,{"disambiguationData":[OSD([sQuery(id+"F0.wireOp",EDGE,"E1.bottom")])],"isStart":false});
            fillet(context, id + "F15", {"entities" : qUnion([Q0]), "radius" : 2 * mm, "tangentPropagation" : true, "allowEdgeOverflow" : false});
        }
        {
            var Q0;
            {var subQ0=sQuery(id+"F0.wireOp",EDGE,"E21.filletArc");var subQ1=sQuery(id+"F0.wireOp",EDGE,"E7");var subQ2=sQuery(id+"F0.wireOp",EDGE,"E6");var subQ3=sQuery(id+"F0.wireOp",EDGE,"E5");var subQ4=sQuery(id+"F0.wireOp",EDGE,"E4");var subQ5=sQuery(id+"F0.wireOp",EDGE,"E22.filletArc");var subQ6=sQuery(id+"F0.wireOp",EDGE,"E1.bottom");var subQ7=sQuery(id+"F0.wireOp",EDGE,"E1.right");var subQ8=sQuery(id+"F0.wireOp",EDGE,"E1.top");var subQ9=sQuery(id+"F0.wireOp",EDGE,"E1.left");var subQ10=sQuery(id+"F0.wireOp",EDGE,"E23.filletArc");var subQ11=sQuery(id+"F0.wireOp",EDGE,"E24.filletArc");Q0=makeQuery(id+"F2.boolean.opBoolean","SPLIT",FACE,{"disambiguationData":[TD([makeQuery(id+"F1.opExtrude","SWEPT_FACE",FACE,{"disambiguationData":[OSD([subQ6])]})])],"derivedFrom":makeQuery(id+"F1.opExtrude","CAP_FACE",FACE,{"disambiguationData":[OSD([subQ6,subQ8,subQ9,subQ7,subQ4,subQ3,subQ2,subQ1,subQ0,subQ5,subQ10,subQ11])],"isStart":true})});}
            var sketch = newSketch(context, id + "F16", { "sketchPlane" : qUnion([Q0])});
            skLineSegment(sketch, "E79", {"start": v(0, 90) * mm, "end": v(0, 120) * mm, "construction": true});
            skCircle(sketch, "E80", {"center": v(0, 120) * mm, "radius": 6 * mm});
            skCircle(sketch, "E81", {"center": v(0, 120) * mm, "radius": 15 * mm});
            skLineSegment(sketch, "E82", {"start": v(0, 120) * mm, "end": v(-15, 120) * mm, "construction": true});
            skLineSegment(sketch, "E83", {"start": v(-15, 120) * mm, "end": v(15, 120) * mm, "construction": true});
            skLineSegment(sketch, "E84", {"start": v(-15, 120) * mm, "end": v(-15, 108) * mm});
            skLineSegment(sketch, "E85", {"start": v(15, 120) * mm, "end": v(15, 108) * mm});
            skLineSegment(sketch, "E86", {"start": v(-15, 108) * mm, "end": v(-33, 90) * mm});
            skLineSegment(sketch, "E87", {"start": v(15, 108) * mm, "end": v(33, 90) * mm});
            skLineSegment(sketch, "E88", {"start": v(-80, 0) * mm, "end": v(80, 0) * mm, "construction": true});
            skCircle(sketch, "E89.MirrorC", {"center": v(0, -120) * mm, "radius": 15 * mm});
            skLineSegment(sketch, "E90.MirrorCS", {"start": v(-15, -108) * mm, "end": v(-33, -90) * mm});
            skLineSegment(sketch, "E91.MirrorCS", {"start": v(15, -108) * mm, "end": v(33, -90) * mm});
            skCircle(sketch, "E92.MirrorC", {"center": v(0, -120) * mm, "radius": 6 * mm});
            skLineSegment(sketch, "E93.MirrorCS", {"start": v(-15, -120) * mm, "end": v(-15, -108) * mm});
            skLineSegment(sketch, "E94.MirrorCS", {"start": v(15, -120) * mm, "end": v(15, -108) * mm});
            skSolve(sketch);
        }
        {
            var Q0;
            Q0=makeQuery(id+"F16.imprint","IMPRINT",FACE,{"disambiguationData":[TD([[makeQuery(id+"F16.imprint","IMPRINT",EDGE,{"derivedFrom":sQuery(id+"F16.wireOp",EDGE,"E80")}),-1.0]])]});
            var Q1;
            {var subQ4=sQuery(id+"F16.wireOp",EDGE,"E84");Q1=makeQuery(id+"F16.imprint","IMPRINT",FACE,{"disambiguationData":[TD([[makeQuery(id+"F16.imprint","IMPRINT",EDGE,{"derivedFrom":subQ4}),1.0]])]});}
            var Q2;
            Q2=makeQuery(id+"F16.imprint","IMPRINT",FACE,{"disambiguationData":[TD([[makeQuery(id+"F16.imprint","IMPRINT",EDGE,{"derivedFrom":makeQuery(id+"F1.opExtrude","CAP_EDGE",EDGE,{"disambiguationData":[OSD([sQuery(id+"F0.wireOp",EDGE,"E1.left")])],"isStart":true})}),-1.0]])]});
            var Q3;
            {var subQ1=sQuery(id+"F16.wireOp",EDGE,"E90.MirrorCS");Q3=makeQuery(id+"F16.imprint","IMPRINT",FACE,{"disambiguationData":[TD([[makeQuery(id+"F16.imprint","IMPRINT",EDGE,{"derivedFrom":subQ1}),-1.0]])]});}
            var Q4;
            Q4=makeQuery(id+"F16.imprint","IMPRINT",FACE,{"disambiguationData":[TD([[makeQuery(id+"F16.imprint","IMPRINT",EDGE,{"derivedFrom":sQuery(id+"F16.wireOp",EDGE,"E92.MirrorC")}),1.0]])]});
            var Q5;
            Q5=makeQuery(id+"F2.opExtrude","CAP_FACE",FACE,{"disambiguationData":[OSD([sQuery(id+"F0.wireOp",EDGE,"E12"),sQuery(id+"F0.wireOp",EDGE,"E13"),sQuery(id+"F0.wireOp",EDGE,"E14"),sQuery(id+"F0.wireOp",EDGE,"E15"),sQuery(id+"F0.wireOp",EDGE,"E17.filletArc"),sQuery(id+"F0.wireOp",EDGE,"E18.filletArc"),sQuery(id+"F0.wireOp",EDGE,"E19.filletArc"),sQuery(id+"F0.wireOp",EDGE,"E20.filletArc"),sQuery(id+"F0.wireOp",EDGE,"E25.0"),sQuery(id+"F0.wireOp",EDGE,"E25.1"),sQuery(id+"F0.wireOp",EDGE,"E25.2"),sQuery(id+"F0.wireOp",EDGE,"E25.3"),sQuery(id+"F0.wireOp",EDGE,"E25.4"),sQuery(id+"F0.wireOp",EDGE,"E25.5"),sQuery(id+"F0.wireOp",EDGE,"E25.6"),sQuery(id+"F0.wireOp",EDGE,"E25.7")])],"isStart":false});
            extrude(context, id + "F17", {"entities" : qUnion([Q0, Q1, Q2, Q3, Q4]), "endBound" : BoundingType.UP_TO_SURFACE, "endBoundEntityFace" : qUnion([Q5]), "depth" : 25 * mm});
        }
    });
